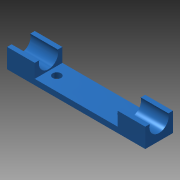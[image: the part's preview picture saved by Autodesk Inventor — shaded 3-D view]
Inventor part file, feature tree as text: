
AUTODESK INVENTOR PART (.ipt)
format: ipt  version: 2013 SP2 (Build 170200200, 200)  size: 134,144 bytes
history: native  units: mm
features: extrude x6, sketch x5
ambient origin geometry x8: Origin, YZ Plane, XZ Plane, XY Plane, X Axis, Y Axis, Z Axis, Center Point
bodies: Solid1 (feature_tree)
feature tree (11):
  extrude  "Extrusion1"  Depth=10.0mm
  extrude  "Extrusion2"  Depth=7.0mm
  extrude  "Extrusion3"  Depth=12.0mm
  extrude  "Extrusion4"  Depth=12.0mm
  extrude  "Extrusion6"  Depth=12.0mm
  extrude  "Extrusion5"  Depth=6.0mm
  sketch  "Sketch1"  dims[d0=50.0mm d1=10.0mm]
  sketch  "Sketch2"  dims[d2=7.0mm d3=0.0mm d4=7.0mm]
  sketch  "Sketch3"  dims[d5=10.0mm d6=0.0mm d15=12.0mm]
  sketch  "Sketch4"  dims[d16=6.0mm d17=12.0mm]
  sketch  "Sketch6"  dims[d18=6.0mm d19=12.0mm d20=6.0mm d21=12.0mm d22=6.0mm d23=3.0mm d24=3.0mm d25=3.0mm d26=3.0mm d27=3.0mm d28=0.0mm d29=30.0mm d31=5.0mm d32=0.0mm d33=1.0mm d34=3.0mm d35=3.0mm d38=10.0mm d39=0.0mm d41=3.0mm d42=2.0mm d43=0.0mm d44=8.0mm d45=3.0mm d46=3.0mm]
